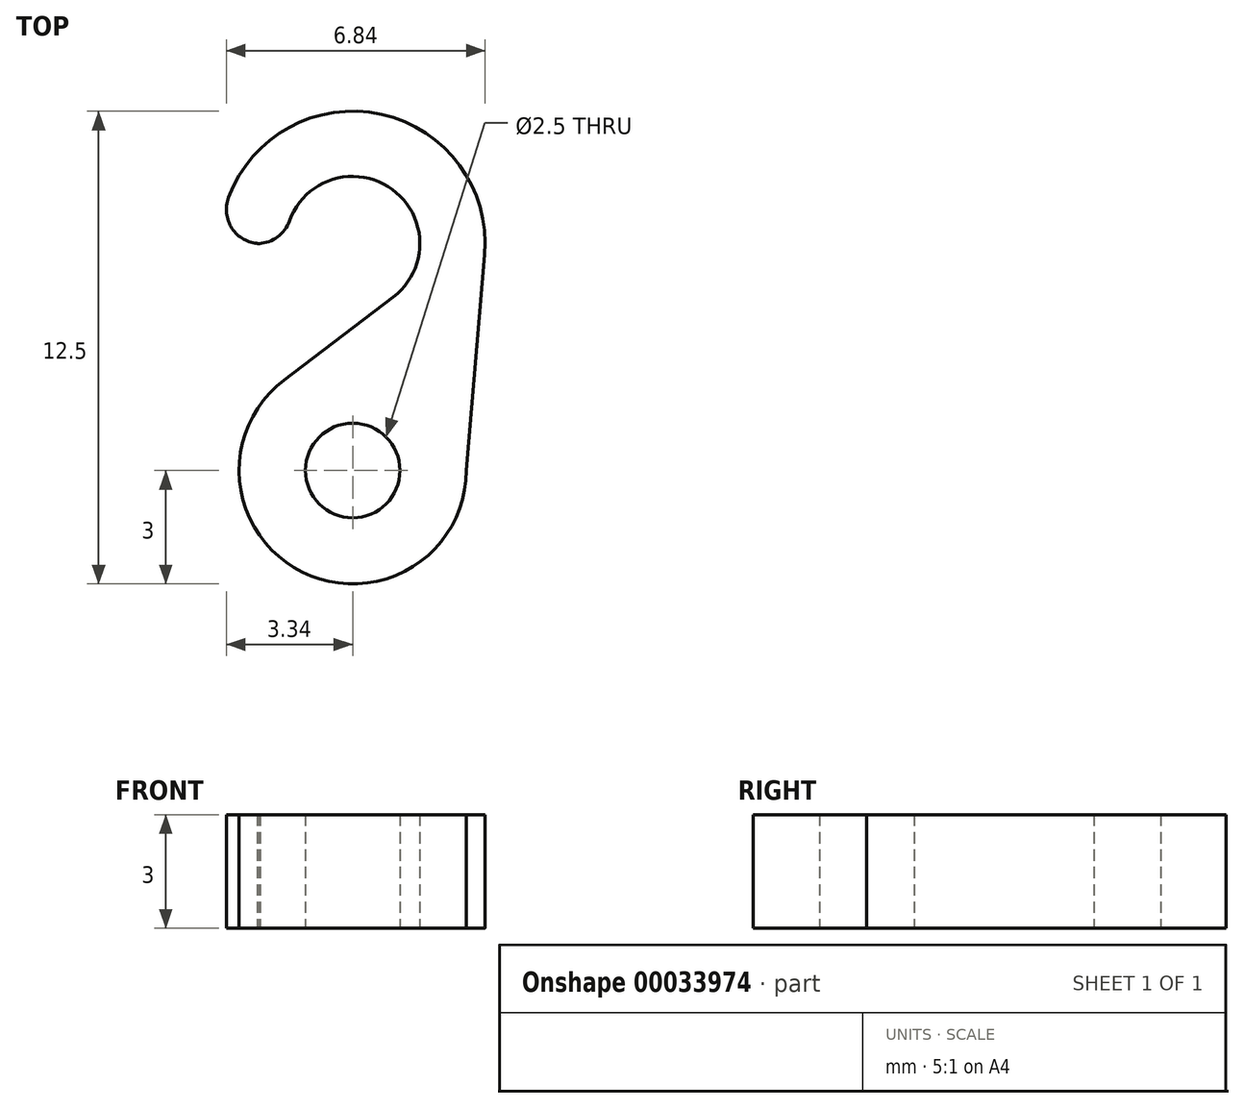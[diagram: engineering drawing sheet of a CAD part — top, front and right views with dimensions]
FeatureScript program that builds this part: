
annotation { "Feature Type Name" : "Feature", "Feature Type Description" : "" }
export const myFeature = defineFeature(function(context is Context, id is Id, definition is map)
    precondition{}
    {
        {
            var Q0;
            Q0=qCreatedBy(makeId("Top.planeOp"),FACE);
            var sketch = newSketch(context, id + "F0", { "sketchPlane" : qUnion([Q0])});
            skCircle(sketch, "E0", {"center": v(0, 0) * mm, "radius": 1.25 * mm});
            skArc(sketch, "E1", {"start": v(-1.82, 2.39) * mm, "mid": v(-1.33, -2.69) * mm, "end": v(3, 0) * mm});
            skArc(sketch, "E2", {"start": v(-1.33, 2.76) * mm, "mid": v(-1.29, 2.74) * mm, "end": v(-1.25, 2.73) * mm});
            skArc(sketch, "E3", {"start": v(1.07, 4.59) * mm, "mid": v(1.05, 7.43) * mm, "end": v(-1.67, 6.6) * mm});
            skLineSegment(sketch, "E4", {"start": v(-2.44, 6) * mm, "end": v(-2.52, 6) * mm});
            skLineSegment(sketch, "E5", {"start": v(3, 0) * mm, "end": v(3.51, 6) * mm});
            skLineSegment(sketch, "E6", {"start": v(-1.82, 2.39) * mm, "end": v(1.07, 4.59) * mm});
            skArc(sketch, "E7.trimOffspring", {"start": v(3.49, 5.7) * mm, "mid": v(0.76, 9.42) * mm, "end": v(-3.28, 7.21) * mm});
            skPoint(sketch, "E8.visualSharp", {"position": v(-3.5, 6) * mm});
            skArc(sketch, "E8.filletArc", {"start": v(-3.28, 7.21) * mm, "mid": v(-3.18, 6.39) * mm, "end": v(-2.44, 6) * mm});
            skPoint(sketch, "E9.visualSharp", {"position": v(-1.77, 6) * mm});
            skArc(sketch, "E9.filletArc", {"start": v(-2.52, 6) * mm, "mid": v(-2, 6.16) * mm, "end": v(-1.67, 6.6) * mm});
            skSolve(sketch);
        }
        {
            var Q0;
            Q0 = qSketchRegion(id + "F0", true);
            extrude(context, id + "F1", {"entities" : qUnion([Q0]), "depth" : 3 * mm});
        }
    });
